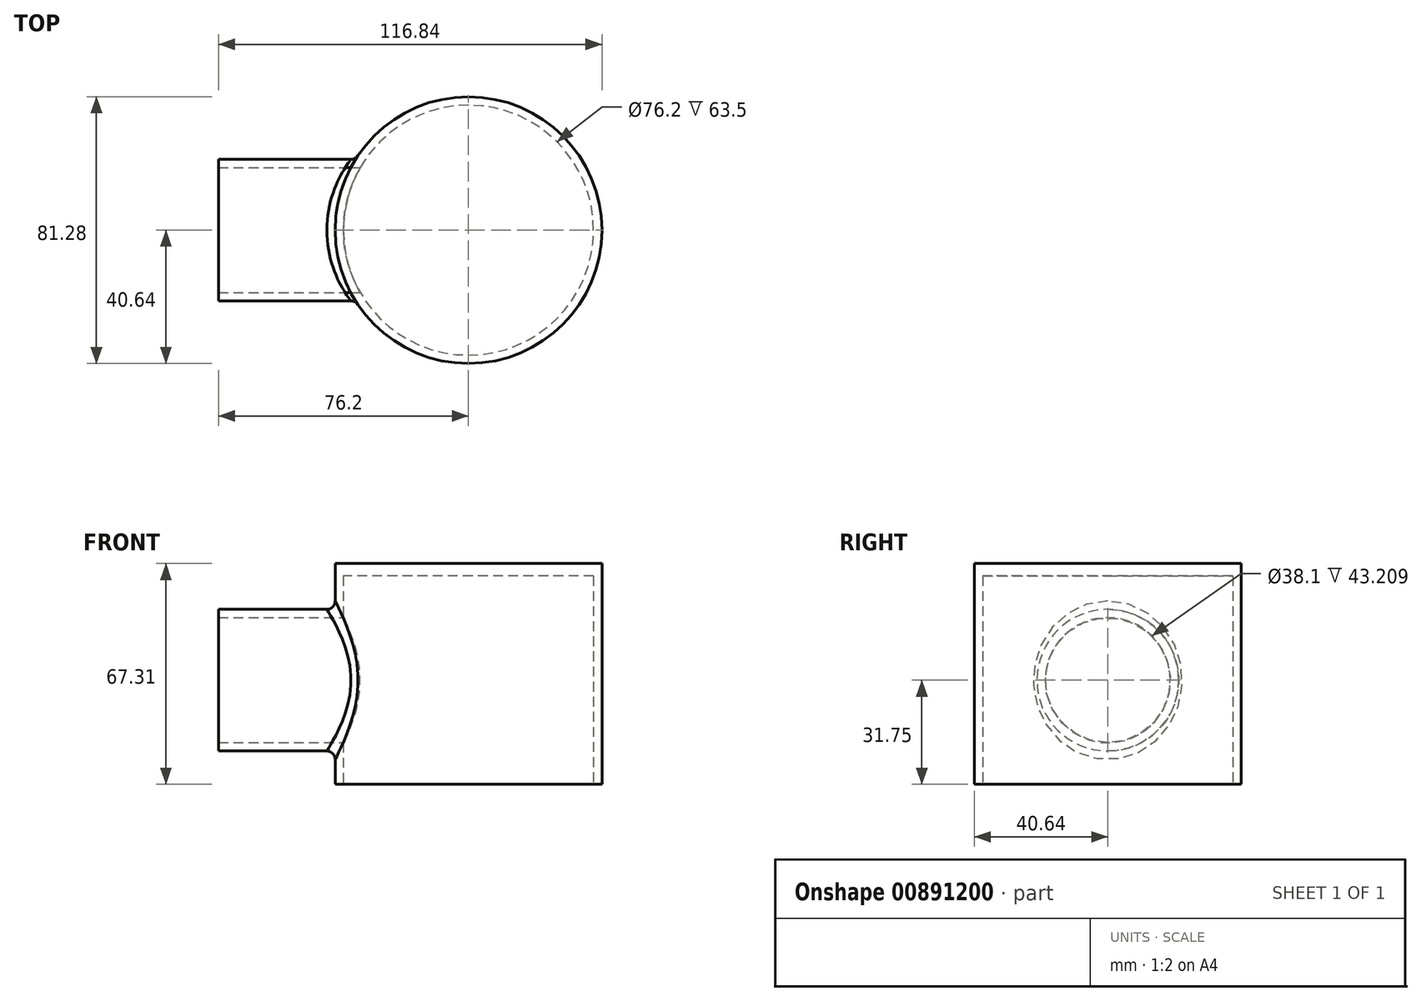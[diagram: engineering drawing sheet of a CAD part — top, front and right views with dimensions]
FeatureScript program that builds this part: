
annotation { "Feature Type Name" : "Feature", "Feature Type Description" : "" }
export const myFeature = defineFeature(function(context is Context, id is Id, definition is map)
    precondition{}
    {
        {
            var Q0;
            Q0=qCreatedBy(makeId("Top.planeOp"),FACE);
            var sketch = newSketch(context, id + "F0", { "sketchPlane" : qUnion([Q0])});
            skCircle(sketch, "E0", {"center": v(0, 0) * mm, "radius": 38.1 * mm});
            skCircle(sketch, "E1", {"center": v(0, 0) * mm, "radius": 40.64 * mm});
            skSolve(sketch);
        }
        {
            var Q0;
            Q0 = qSketchRegion(id + "F0", true);
            extrude(context, id + "F1", {"entities" : qUnion([Q0]), "depth" : 63.5 * mm, "offsetDistance" : 25.4 * mm});
        }
        {
            var Q0;
            Q0=qCreatedBy(makeId("Right.planeOp"),FACE);
            var sketch = newSketch(context, id + "F2", { "sketchPlane" : qUnion([Q0])});
            skLineSegment(sketch, "E2", {"start": v(0, 0) * mm, "end": v(0, 63.5) * mm, "construction": true});
            skCircle(sketch, "E3", {"center": v(0, 31.75) * mm, "radius": 19.05 * mm});
            skSolve(sketch);
        }
        {
            var Q0;
            Q0 = qSketchRegion(id + "F2", true);
            extrude(context, id + "F3", {"entities" : qUnion([Q0]), "operationType" : NewBodyOperationType.REMOVE, "oppositeDirection" : true, "depth" : 63 * mm, "offsetDistance" : 25.4 * mm});
        }
        {
            var Q0;
            Q0=qCreatedBy(makeId("Right.planeOp"),FACE);
            var sketch = newSketch(context, id + "F4", { "sketchPlane" : qUnion([Q0])});
            skLineSegment(sketch, "E4", {"start": v(0, 0) * mm, "end": v(0, 63.5) * mm, "construction": true});
            skCircle(sketch, "E5", {"center": v(0, 31.75) * mm, "radius": 21.59 * mm});
            skCircle(sketch, "E6", {"center": v(0, 31.75) * mm, "radius": 19.05 * mm});
            skSolve(sketch);
        }
        {
            var Q0;
            Q0 = qSketchRegion(id + "F4", true);
            extrude(context, id + "F5", {"entities" : qUnion([Q0]), "operationType" : NewBodyOperationType.ADD, "oppositeDirection" : true, "depth" : 76.2 * mm, "offsetDistance" : 25.4 * mm});
        }
        {
            var Q0;
            Q0=qCreatedBy(makeId("Top.planeOp"),FACE);
            var sketch = newSketch(context, id + "F6", { "sketchPlane" : qUnion([Q0])});
            skCircle(sketch, "E7", {"center": v(0, 0) * mm, "radius": 38.1 * mm});
            skSolve(sketch);
        }
        {
            var Q0;
            Q0 = qSketchRegion(id + "F6", true);
            extrude(context, id + "F7", {"entities" : qUnion([Q0]), "operationType" : NewBodyOperationType.REMOVE, "depth" : 108.46 * mm, "offsetDistance" : 25.4 * mm});
        }
        {
            var Q0;
            Q0=makeQuery(id+"F1.opExtrude","CAP_FACE",FACE,{"disambiguationData":[OSD([sQuery(id+"F0.wireOp",EDGE,"E0"),sQuery(id+"F0.wireOp",EDGE,"E1")])],"isStart":false});
            var sketch = newSketch(context, id + "F8", { "sketchPlane" : qUnion([Q0])});
            skCircle(sketch, "E8", {"center": v(0, 0) * mm, "radius": 40.64 * mm});
            skSolve(sketch);
        }
        {
            var Q0;
            Q0 = qSketchRegion(id + "F8", true);
            extrude(context, id + "F9", {"entities" : qUnion([Q0]), "operationType" : NewBodyOperationType.ADD, "depth" : 3.8 * mm, "offsetDistance" : 25.4 * mm});
        }
        {
            var Q0;
            Q0=makeQuery(id+"F5.boolean.opBoolean","INTERSECT",EDGE,{"derivedFrom":[makeQuery(id+"F1.opExtrude","SWEPT_FACE",FACE,{"disambiguationData":[OSD([sQuery(id+"F0.wireOp",EDGE,"E1")])]}),makeQuery(id+"F5.opExtrude","SWEPT_FACE",FACE,{"disambiguationData":[OSD([sQuery(id+"F4.wireOp",EDGE,"E5")])]})]});
            fillet(context, id + "F10", {"entities" : qUnion([Q0]), "radius" : 2.54 * mm, "tangentPropagation" : true, "allowEdgeOverflow" : false});
        }
    });
